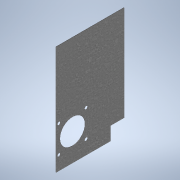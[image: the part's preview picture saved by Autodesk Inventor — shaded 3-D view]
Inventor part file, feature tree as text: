
AUTODESK INVENTOR PART (.ipt)
format: ipt  version: 2022.1 (Build 261234000, 234)  size: 122,368 bytes
history: native  units: mm (DEFAULTED — no unit token found)
features: other x8, extrude x1
bodies: Body1 (feature_tree)
feature tree (9):
  other  "Sólido1"
  other  "Origen"
  extrude  "Extrusión1"  Depth=75.0mm
  other  "Plano YZ"
  other  "Plano XZ"
  other  "Plano XY"
  other  "Eje X"
  other  "Eje Y"
  other  "Eje Z"
